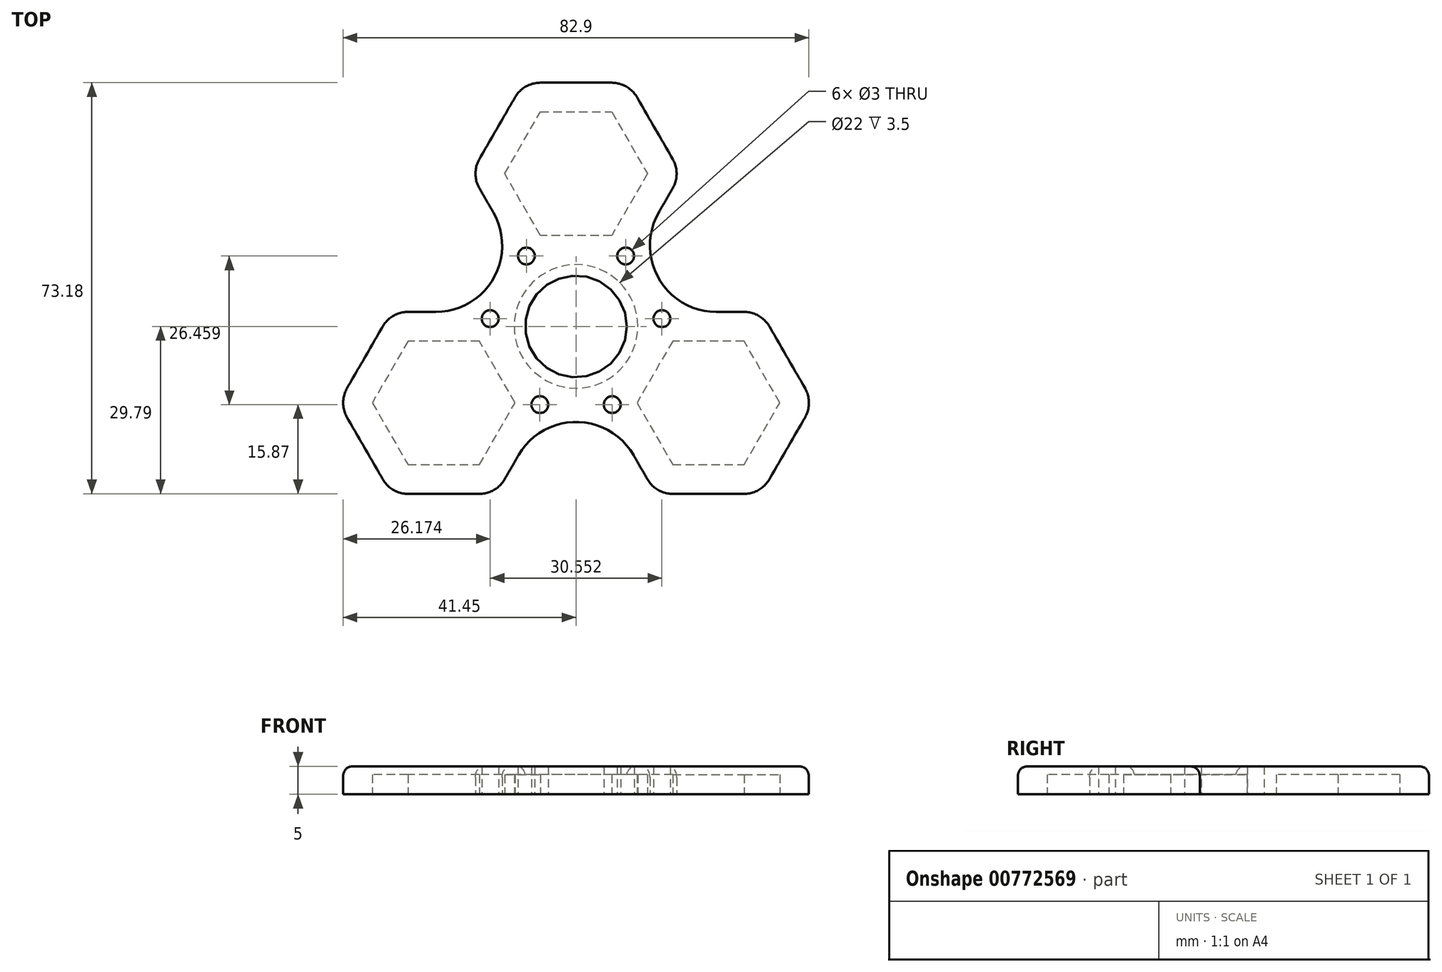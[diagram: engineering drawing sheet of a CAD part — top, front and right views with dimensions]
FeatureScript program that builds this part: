
annotation { "Feature Type Name" : "Feature", "Feature Type Description" : "" }
export const myFeature = defineFeature(function(context is Context, id is Id, definition is map)
    precondition{}
    {
        {
            var Q0;
            Q0=qCreatedBy(makeId("Top.planeOp"),FACE);
            var sketch = newSketch(context, id + "F0", { "sketchPlane" : qUnion([Q0])});
            skLineSegment(sketch, "E0.0", {"start": v(0, 27.2) * mm, "end": v(23.55, -13.6) * mm, "construction": true});
            skLineSegment(sketch, "E0.1", {"start": v(23.55, -13.6) * mm, "end": v(-23.55, -13.6) * mm, "construction": true});
            skLineSegment(sketch, "E0.2", {"start": v(-23.55, -13.6) * mm, "end": v(0, 27.2) * mm, "construction": true});
            skPoint(sketch, "E0.0.midPoint", {"position": v(11.78, 6.8) * mm});
            skLineSegment(sketch, "E1", {"start": v(-23.55, -13.6) * mm, "end": v(11.78, 6.8) * mm, "construction": true});
            skLineSegment(sketch, "E2", {"start": v(-11.78, 6.8) * mm, "end": v(23.55, -13.6) * mm, "construction": true});
            skCircle(sketch, "E3", {"center": v(0, 0) * mm, "radius": 11 * mm});
            skCircle(sketch, "E4.cCircle", {"center": v(0, 27.2) * mm, "radius": 12.7 * mm, "construction": true});
            skLineSegment(sketch, "E4.0", {"start": v(6.35, 16.2) * mm, "end": v(-6.35, 16.2) * mm});
            skLineSegment(sketch, "E4.1", {"start": v(-6.35, 16.2) * mm, "end": v(-12.7, 27.2) * mm});
            skLineSegment(sketch, "E4.2", {"start": v(-12.7, 27.2) * mm, "end": v(-6.35, 38.2) * mm});
            skLineSegment(sketch, "E4.3", {"start": v(-6.35, 38.2) * mm, "end": v(6.35, 38.2) * mm});
            skLineSegment(sketch, "E4.4", {"start": v(6.35, 38.2) * mm, "end": v(12.7, 27.2) * mm});
            skLineSegment(sketch, "E4.5", {"start": v(12.7, 27.2) * mm, "end": v(6.35, 16.2) * mm});
            skLineSegment(sketch, "E5.MirrorCS", {"start": v(10.85, -13.6) * mm, "end": v(17.2, -24.6) * mm});
            skLineSegment(sketch, "E6.MirrorCS", {"start": v(17.2, -24.6) * mm, "end": v(29.9, -24.6) * mm});
            skLineSegment(sketch, "E7.MirrorCS", {"start": v(29.9, -24.6) * mm, "end": v(36.25, -13.6) * mm});
            skLineSegment(sketch, "E8.MirrorCS", {"start": v(36.25, -13.6) * mm, "end": v(29.9, -2.6) * mm});
            skLineSegment(sketch, "E9.MirrorCS", {"start": v(29.9, -2.6) * mm, "end": v(17.2, -2.6) * mm});
            skLineSegment(sketch, "E10.MirrorCS", {"start": v(17.2, -2.6) * mm, "end": v(10.85, -13.6) * mm});
            skLineSegment(sketch, "E11.MirrorCS", {"start": v(-17.2, -2.6) * mm, "end": v(-29.9, -2.6) * mm});
            skLineSegment(sketch, "E12.MirrorCS", {"start": v(-29.9, -2.6) * mm, "end": v(-36.25, -13.6) * mm});
            skLineSegment(sketch, "E13.MirrorCS", {"start": v(-36.25, -13.6) * mm, "end": v(-29.9, -24.6) * mm});
            skLineSegment(sketch, "E14.MirrorCS", {"start": v(-29.9, -24.6) * mm, "end": v(-17.2, -24.6) * mm});
            skLineSegment(sketch, "E15.MirrorCS", {"start": v(-17.2, -24.6) * mm, "end": v(-10.85, -13.6) * mm});
            skLineSegment(sketch, "E16.MirrorCS", {"start": v(-10.85, -13.6) * mm, "end": v(-17.2, -2.6) * mm});
            skCircle(sketch, "E17.cCircle", {"center": v(0, 27.2) * mm, "radius": 18.7 * mm, "construction": true});
            skLineSegment(sketch, "E17.0", {"start": v(-9.35, 11) * mm, "end": v(-17.2, 24.6) * mm});
            skLineSegment(sketch, "E17.1", {"start": v(-17.2, 29.8) * mm, "end": v(-10.85, 40.8) * mm});
            skLineSegment(sketch, "E17.2", {"start": v(-6.35, 43.39) * mm, "end": v(6.35, 43.39) * mm});
            skLineSegment(sketch, "E17.3", {"start": v(10.85, 40.8) * mm, "end": v(17.2, 29.8) * mm});
            skLineSegment(sketch, "E17.4", {"start": v(17.2, 24.6) * mm, "end": v(9.35, 11) * mm});
            skLineSegment(sketch, "E17.5", {"start": v(9.35, 11) * mm, "end": v(-9.35, 11) * mm, "construction": true});
            skLineSegment(sketch, "E18.MirrorCS", {"start": v(14.2, 2.6) * mm, "end": v(4.85, -13.6) * mm, "construction": true});
            skLineSegment(sketch, "E19.MirrorCS", {"start": v(29.9, 2.6) * mm, "end": v(14.2, 2.6) * mm});
            skLineSegment(sketch, "E20.MirrorCS", {"start": v(40.75, -11) * mm, "end": v(34.4, 0) * mm});
            skLineSegment(sketch, "E21.MirrorCS", {"start": v(34.4, -27.2) * mm, "end": v(40.75, -16.2) * mm});
            skLineSegment(sketch, "E22.MirrorCS", {"start": v(17.2, -29.8) * mm, "end": v(29.9, -29.8) * mm});
            skLineSegment(sketch, "E23.MirrorCS", {"start": v(4.85, -13.6) * mm, "end": v(12.7, -27.2) * mm});
            skLineSegment(sketch, "E24.MirrorCS", {"start": v(-14.2, 2.6) * mm, "end": v(-29.9, 2.6) * mm});
            skLineSegment(sketch, "E25.MirrorCS", {"start": v(-34.4, 0) * mm, "end": v(-40.75, -11) * mm});
            skLineSegment(sketch, "E26.MirrorCS", {"start": v(-40.75, -16.2) * mm, "end": v(-34.4, -27.2) * mm});
            skLineSegment(sketch, "E27.MirrorCS", {"start": v(-29.9, -29.8) * mm, "end": v(-17.2, -29.8) * mm});
            skLineSegment(sketch, "E28.MirrorCS", {"start": v(-12.7, -27.2) * mm, "end": v(-4.85, -13.6) * mm});
            skLineSegment(sketch, "E29.MirrorCS", {"start": v(-4.85, -13.6) * mm, "end": v(-14.2, 2.6) * mm, "construction": true});
            skArc(sketch, "E30", {"start": v(-14.72, 20.3) * mm, "mid": v(-14.72, 8.5) * mm, "end": v(-24.95, 2.6) * mm});
            skLineSegment(sketch, "E31", {"start": v(-9.53, 5.5) * mm, "end": v(-14.72, 8.5) * mm, "construction": true});
            skLineSegment(sketch, "E32", {"start": v(-12.7, 27.2) * mm, "end": v(-18.7, 27.2) * mm, "construction": true});
            skArc(sketch, "E33.MirrorCS", {"start": v(10.22, -22.9) * mm, "mid": v(0, -17) * mm, "end": v(-10.22, -22.9) * mm});
            skArc(sketch, "E34.MirrorCS", {"start": v(24.95, 2.6) * mm, "mid": v(14.72, 8.5) * mm, "end": v(14.72, 20.3) * mm});
            skPoint(sketch, "E35.visualSharp", {"position": v(-18.7, 27.2) * mm});
            skArc(sketch, "E35.filletArc", {"start": v(-17.2, 29.8) * mm, "mid": v(-17.9, 27.2) * mm, "end": v(-17.2, 24.6) * mm});
            skPoint(sketch, "E36.visualSharp", {"position": v(-9.35, 43.39) * mm});
            skArc(sketch, "E36.filletArc", {"start": v(-6.35, 43.39) * mm, "mid": v(-8.95, 42.7) * mm, "end": v(-10.85, 40.8) * mm});
            skPoint(sketch, "E37.visualSharp", {"position": v(9.35, 43.39) * mm});
            skArc(sketch, "E37.filletArc", {"start": v(10.85, 40.8) * mm, "mid": v(8.95, 42.7) * mm, "end": v(6.35, 43.39) * mm});
            skPoint(sketch, "E38.visualSharp", {"position": v(18.7, 27.2) * mm});
            skArc(sketch, "E38.filletArc", {"start": v(17.2, 24.6) * mm, "mid": v(17.9, 27.2) * mm, "end": v(17.2, 29.8) * mm});
            skPoint(sketch, "E39.visualSharp", {"position": v(-32.9, 2.6) * mm});
            skArc(sketch, "E39.filletArc", {"start": v(-29.9, 2.6) * mm, "mid": v(-32.5, 1.9) * mm, "end": v(-34.4, 0) * mm});
            skPoint(sketch, "E40.visualSharp", {"position": v(-42.25, -13.6) * mm});
            skArc(sketch, "E40.filletArc", {"start": v(-40.75, -11) * mm, "mid": v(-41.45, -13.6) * mm, "end": v(-40.75, -16.2) * mm});
            skPoint(sketch, "E41.visualSharp", {"position": v(-32.9, -29.8) * mm});
            skArc(sketch, "E41.filletArc", {"start": v(-34.4, -27.2) * mm, "mid": v(-32.5, -29.1) * mm, "end": v(-29.9, -29.8) * mm});
            skPoint(sketch, "E42.visualSharp", {"position": v(-14.2, -29.8) * mm});
            skArc(sketch, "E42.filletArc", {"start": v(-17.2, -29.8) * mm, "mid": v(-14.6, -29.1) * mm, "end": v(-12.7, -27.2) * mm});
            skPoint(sketch, "E43.visualSharp", {"position": v(14.2, -29.8) * mm});
            skArc(sketch, "E43.filletArc", {"start": v(12.7, -27.2) * mm, "mid": v(14.6, -29.1) * mm, "end": v(17.2, -29.8) * mm});
            skPoint(sketch, "E44.visualSharp", {"position": v(32.9, -29.8) * mm});
            skArc(sketch, "E44.filletArc", {"start": v(29.9, -29.8) * mm, "mid": v(32.5, -29.1) * mm, "end": v(34.4, -27.2) * mm});
            skPoint(sketch, "E45.visualSharp", {"position": v(42.25, -13.6) * mm});
            skArc(sketch, "E45.filletArc", {"start": v(40.75, -16.2) * mm, "mid": v(41.45, -13.6) * mm, "end": v(40.75, -11) * mm});
            skPoint(sketch, "E46.visualSharp", {"position": v(32.9, 2.6) * mm});
            skArc(sketch, "E46.filletArc", {"start": v(34.4, 0) * mm, "mid": v(32.5, 1.9) * mm, "end": v(29.9, 2.6) * mm});
            skLineSegment(sketch, "E47", {"start": v(-17.2, -2.6) * mm, "end": v(-10.87, 1.7) * mm, "construction": true});
            skLineSegment(sketch, "E48", {"start": v(-10.87, 1.7) * mm, "end": v(-17.76, 5.04) * mm, "construction": true});
            skLineSegment(sketch, "E49", {"start": v(-17.76, 5.04) * mm, "end": v(-17.2, -2.6) * mm, "construction": true});
            skLineSegment(sketch, "E50", {"start": v(-14.31, 3.37) * mm, "end": v(-17.2, -2.6) * mm, "construction": true});
            skLineSegment(sketch, "E51", {"start": v(-17.48, 1.22) * mm, "end": v(-10.87, 1.7) * mm, "construction": true});
            skLineSegment(sketch, "E52", {"start": v(-17.76, 5.04) * mm, "end": v(-15.28, 1.38) * mm, "construction": true});
            skCircle(sketch, "E53", {"center": v(-15.28, 1.38) * mm, "radius": 1.5 * mm});
            skCircle(sketch, "E54.MirrorC", {"center": v(-8.83, 12.54) * mm, "radius": 1.5 * mm});
            skCircle(sketch, "E55.MirrorC", {"center": v(-6.44, -13.92) * mm, "radius": 1.5 * mm});
            skCircle(sketch, "E56.MirrorC", {"center": v(6.44, -13.92) * mm, "radius": 1.5 * mm});
            skCircle(sketch, "E57.MirrorC", {"center": v(15.28, 1.38) * mm, "radius": 1.5 * mm});
            skCircle(sketch, "E58.MirrorC", {"center": v(8.83, 12.54) * mm, "radius": 1.5 * mm});
            skLineSegment(sketch, "E59", {"start": v(0, 11) * mm, "end": v(0, 9) * mm});
            skCircle(sketch, "E60", {"center": v(0, 0) * mm, "radius": 9 * mm});
            skSolve(sketch);
        }
        {
            var Q0;
            Q0 = qSketchRegion(id + "F0", true);
            var Q1;
            Q1=makeQuery(id+"F0.imprint","IMPRINT",FACE,{"disambiguationData":[TD([[makeQuery(id+"F0.imprint","IMPRINT",EDGE,{"derivedFrom":sQuery(id+"F0.wireOp",EDGE,"E11.MirrorCS")}),1.0]])]});
            var Q2;
            Q2=makeQuery(id+"F0.imprint","IMPRINT",FACE,{"disambiguationData":[TD([[makeQuery(id+"F0.imprint","IMPRINT",EDGE,{"derivedFrom":sQuery(id+"F0.wireOp",EDGE,"E4.0")}),-1.0]])]});
            var Q3;
            Q3=makeQuery(id+"F0.imprint","IMPRINT",FACE,{"disambiguationData":[TD([[makeQuery(id+"F0.imprint","IMPRINT",EDGE,{"derivedFrom":sQuery(id+"F0.wireOp",EDGE,"E5.MirrorCS")}),1.0]])]});
            var Q4;
            Q4=makeQuery(id+"F0.imprint","IMPRINT",FACE,{"disambiguationData":[TD([[makeQuery(id+"F0.imprint","IMPRINT",EDGE,{"derivedFrom":sQuery(id+"F0.wireOp",EDGE,"E3")}),1.0]])]});
            extrude(context, id + "F1", {"entities" : qUnion([Q0, Q1, Q2, Q3, Q4]), "depth" : 5 * mm, "offsetDistance" : 25.4 * mm});
        }
        {
            var Q0;
            Q0=makeQuery(id+"F1.opExtrude","CAP_EDGE",EDGE,{"disambiguationData":[OSD([sQuery(id+"F0.wireOp",EDGE,"E34.MirrorCS")])],"isStart":false});
            var Q1;
            Q1=makeQuery(id+"F1.opExtrude","CAP_EDGE",EDGE,{"disambiguationData":[OSD([sQuery(id+"F0.wireOp",EDGE,"E60")])],"isStart":false});
            fillet(context, id + "F2", {"entities" : qUnion([Q0, Q1]), "radius" : 2 * mm, "tangentPropagation" : true, "rho" : 0.5, "crossSection" : FilletCrossSection.CONIC, "allowEdgeOverflow" : false});
        }
        {
            var Q0;
            Q0=makeQuery(id+"F0.imprint","IMPRINT",FACE,{"disambiguationData":[TD([[makeQuery(id+"F0.imprint","IMPRINT",EDGE,{"derivedFrom":sQuery(id+"F0.wireOp",EDGE,"E5.MirrorCS")}),1.0]])]});
            var Q1;
            Q1=makeQuery(id+"F0.imprint","IMPRINT",FACE,{"disambiguationData":[TD([[makeQuery(id+"F0.imprint","IMPRINT",EDGE,{"derivedFrom":sQuery(id+"F0.wireOp",EDGE,"E11.MirrorCS")}),1.0]])]});
            var Q2;
            Q2=makeQuery(id+"F0.imprint","IMPRINT",FACE,{"disambiguationData":[TD([[makeQuery(id+"F0.imprint","IMPRINT",EDGE,{"derivedFrom":sQuery(id+"F0.wireOp",EDGE,"E4.0")}),-1.0]])]});
            var Q3;
            Q3=makeQuery(id+"F0.imprint","IMPRINT",FACE,{"disambiguationData":[TD([[makeQuery(id+"F0.imprint","IMPRINT",EDGE,{"derivedFrom":sQuery(id+"F0.wireOp",EDGE,"E3")}),1.0]])]});
            extrude(context, id + "F3", {"entities" : qUnion([Q0, Q1, Q2, Q3]), "operationType" : NewBodyOperationType.REMOVE, "depth" : 3.5 * mm, "offsetDistance" : 25.4 * mm});
        }
    });
